# Revit family: METALFIRE_AVENUE_L_MF_1300-85_GHE_1Sa
name_source: partatom
category: Mechanical Equipment
revit_build: Autodesk Revit 2018 (Build: 20190510_1515(x64)
units: mm (PartAtom-declared; Revit-internal decimal feet)

## family parameters
Always vertical = Yes
Cut with Voids When Loaded = No
Host = Wall
OmniClass Number = 23.75.00.00
OmniClass Title = Climate Control (HVAC)
Part Type = Normal
Room Calculation Point = No
Round Connector Dimension = Use Diameter
Shared = No

## types (1)
- MF_1300-85_GHE_1S
    BIM BADGE = https://bim.archiproducts.com
    Description = The Avenue represents the gas-fired high efficiency closed fireplaces in the Metalfire range.
    ENERGY EFFICIENCY CLASS = B
    FINISHING MATERIAL = Painted steel, cast iron
    FRAME MATERIAL = Iron - Metalfire
    HEIGHT = 850 mm
    MATERIAL DESCRIPTION = Iron, galvanized steel
    Manufacturer = METALFIRE
    Model = Avenue
    OUTPUT = 11400 W
    OVERALL DEPTH = 444 mm
    OVERALL HEIGHT = 1120 mm
    OVERALL WIDTH = 1178 mm
    PIPE = 200 mm
    PRODUCT CODE = L MF 1300-85 GHE 1S
    PRODUCT SHEET = https://www.archiproducts.com
    SMOKE EXHAUST = Ø130/200 mm
    TECHNICAL SHEET = https://www.metalfire.eu
    URL = https://www.metalfire.eu
    WEIGHT = 180.00 kg
    WIDTH = 1330 mm

## geometry (parser evidence)
native form markers: Sweep x5
no freeform markers — native parametric forms only
